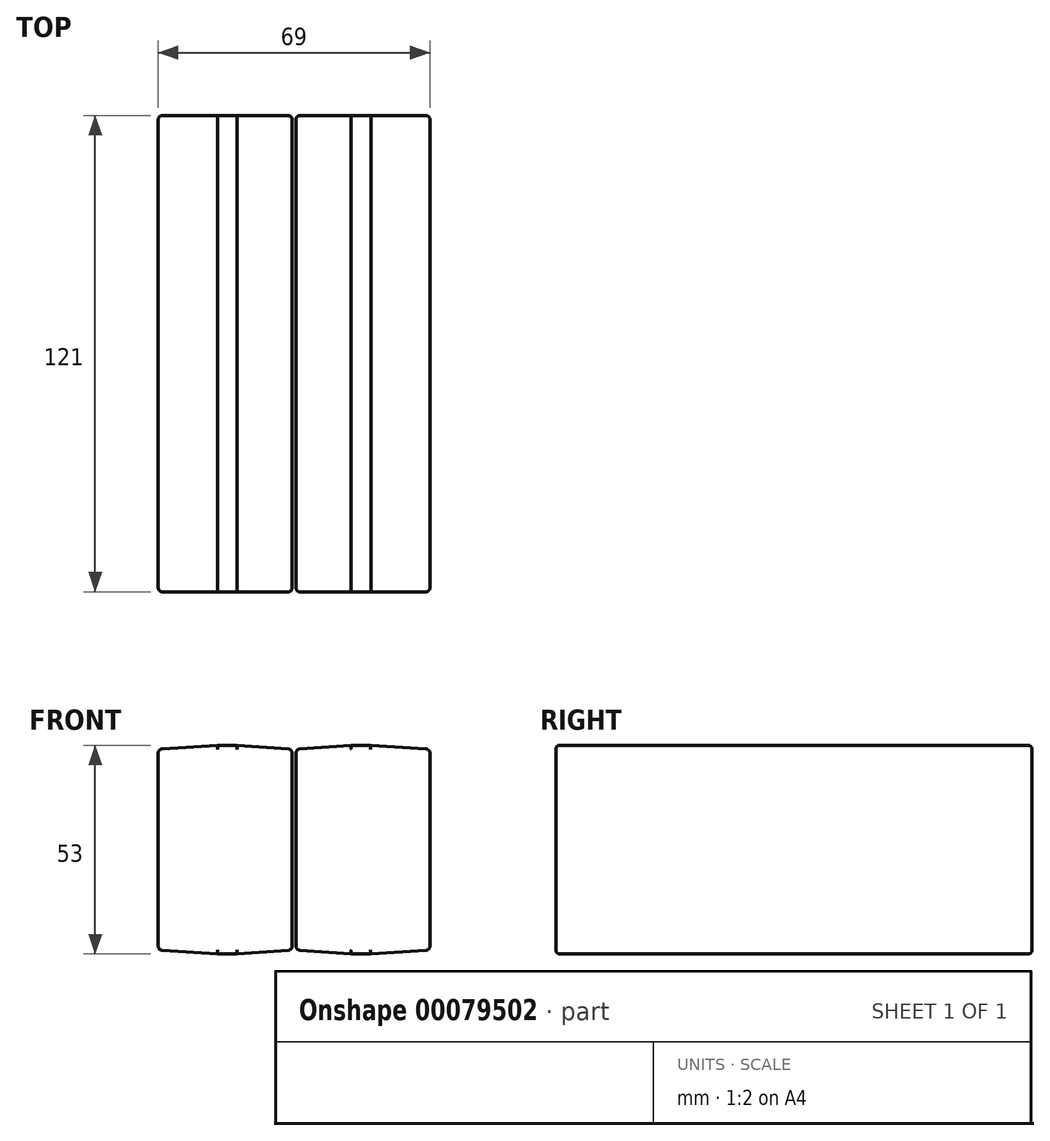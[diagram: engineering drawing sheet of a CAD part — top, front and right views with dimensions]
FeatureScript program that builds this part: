
annotation { "Feature Type Name" : "Feature", "Feature Type Description" : "" }
export const myFeature = defineFeature(function(context is Context, id is Id, definition is map)
    precondition{}
    {
        {
            var Q0;
            Q0=qCreatedBy(makeId("Front.planeOp"),FACE);
            var sketch = newSketch(context, id + "F0", { "sketchPlane" : qUnion([Q0])});
            skLineSegment(sketch, "E0", {"start": v(-34.5, 52) * mm, "end": v(-19.5, 53) * mm});
            skLineSegment(sketch, "E1", {"start": v(-19.5, 53) * mm, "end": v(-14.5, 53) * mm});
            skLineSegment(sketch, "E2", {"start": v(-14.5, 53) * mm, "end": v(-0.5, 52) * mm});
            skLineSegment(sketch, "E3", {"start": v(-43.33, 26.5) * mm, "end": v(16.3, 26.5) * mm, "construction": true});
            skLineSegment(sketch, "E4.MirrorCS", {"start": v(-19.5, 0) * mm, "end": v(-14.5, 0) * mm});
            skLineSegment(sketch, "E5.MirrorCS", {"start": v(-34.5, 1) * mm, "end": v(-19.5, 0) * mm});
            skLineSegment(sketch, "E6.MirrorCS", {"start": v(-14.5, 0) * mm, "end": v(-0.5, 1) * mm});
            skLineSegment(sketch, "E7", {"start": v(-34.5, 52) * mm, "end": v(-34.5, 1) * mm});
            skLineSegment(sketch, "E8", {"start": v(-0.5, 52) * mm, "end": v(-0.5, 1) * mm});
            skLineSegment(sketch, "E9.MirrorCS", {"start": v(34.5, 52) * mm, "end": v(19.5, 53) * mm});
            skLineSegment(sketch, "E10.MirrorCS", {"start": v(19.5, 53) * mm, "end": v(14.5, 53) * mm});
            skLineSegment(sketch, "E11.MirrorCS", {"start": v(14.5, 53) * mm, "end": v(0.5, 52) * mm});
            skLineSegment(sketch, "E12.MirrorCS", {"start": v(19.5, 0) * mm, "end": v(14.5, 0) * mm});
            skLineSegment(sketch, "E13.MirrorCS", {"start": v(34.5, 1) * mm, "end": v(19.5, 0) * mm});
            skLineSegment(sketch, "E14.MirrorCS", {"start": v(14.5, 0) * mm, "end": v(0.5, 1) * mm});
            skLineSegment(sketch, "E15.MirrorCS", {"start": v(34.5, 52) * mm, "end": v(34.5, 1) * mm});
            skLineSegment(sketch, "E16.MirrorCS", {"start": v(0.5, 52) * mm, "end": v(0.5, 1) * mm});
            skSolve(sketch);
        }
        {
            var Q0;
            Q0=makeQuery(id+"F0.imprint","IMPRINT",FACE,{"disambiguationData":[TD([[makeQuery(id+"F0.imprint","IMPRINT",EDGE,{"derivedFrom":sQuery(id+"F0.wireOp",EDGE,"E0")}),-1.0]])]});
            extrude(context, id + "F1", {"entities" : qUnion([Q0]), "oppositeDirection" : true, "depth" : 121 * mm});
        }
        {
            var Q0;
            Q0=makeQuery(id+"F1.opExtrude","SWEPT_FACE",FACE,{"disambiguationData":[OSD([sQuery(id+"F0.wireOp",EDGE,"E8")])]});
            var Q1;
            Q1=makeQuery(id+"F1.opExtrude","SWEPT_FACE",FACE,{"disambiguationData":[OSD([sQuery(id+"F0.wireOp",EDGE,"E7")])]});
            var Q2;
            Q2=makeQuery(id+"F1.opExtrude","CAP_FACE",FACE,{"disambiguationData":[OSD([sQuery(id+"F0.wireOp",EDGE,"E0"),sQuery(id+"F0.wireOp",EDGE,"E1"),sQuery(id+"F0.wireOp",EDGE,"E2"),sQuery(id+"F0.wireOp",EDGE,"E4.MirrorCS"),sQuery(id+"F0.wireOp",EDGE,"E5.MirrorCS"),sQuery(id+"F0.wireOp",EDGE,"E6.MirrorCS"),sQuery(id+"F0.wireOp",EDGE,"E7"),sQuery(id+"F0.wireOp",EDGE,"E8")])],"isStart":true});
            var Q3;
            Q3=makeQuery(id+"F1.opExtrude","CAP_FACE",FACE,{"disambiguationData":[OSD([sQuery(id+"F0.wireOp",EDGE,"E0"),sQuery(id+"F0.wireOp",EDGE,"E1"),sQuery(id+"F0.wireOp",EDGE,"E2"),sQuery(id+"F0.wireOp",EDGE,"E4.MirrorCS"),sQuery(id+"F0.wireOp",EDGE,"E5.MirrorCS"),sQuery(id+"F0.wireOp",EDGE,"E6.MirrorCS"),sQuery(id+"F0.wireOp",EDGE,"E7"),sQuery(id+"F0.wireOp",EDGE,"E8")])],"isStart":false});
            fillet(context, id + "F2", {"entities" : qUnion([Q0, Q1, Q2, Q3]), "radius" : 1 * mm, "tangentPropagation" : true, "allowEdgeOverflow" : false});
        }
        {
            var Q0;
            Q0=makeQuery(id+"F1.opExtrude","SWEPT_BODY",BODY,{"disambiguationData":[OSD([sQuery(id+"F0.wireOp",EDGE,"E0"),sQuery(id+"F0.wireOp",EDGE,"E1"),sQuery(id+"F0.wireOp",EDGE,"E2"),sQuery(id+"F0.wireOp",EDGE,"E4.MirrorCS"),sQuery(id+"F0.wireOp",EDGE,"E5.MirrorCS"),sQuery(id+"F0.wireOp",EDGE,"E6.MirrorCS"),sQuery(id+"F0.wireOp",EDGE,"E7"),sQuery(id+"F0.wireOp",EDGE,"E8")])]});
            var Q1;
            Q1=qCreatedBy(makeId("Right.planeOp"),FACE);
            mirror(context, id + "F3", {"entities" : qUnion([Q0]), "mirrorPlane" : qUnion([Q1])});
        }
    });
